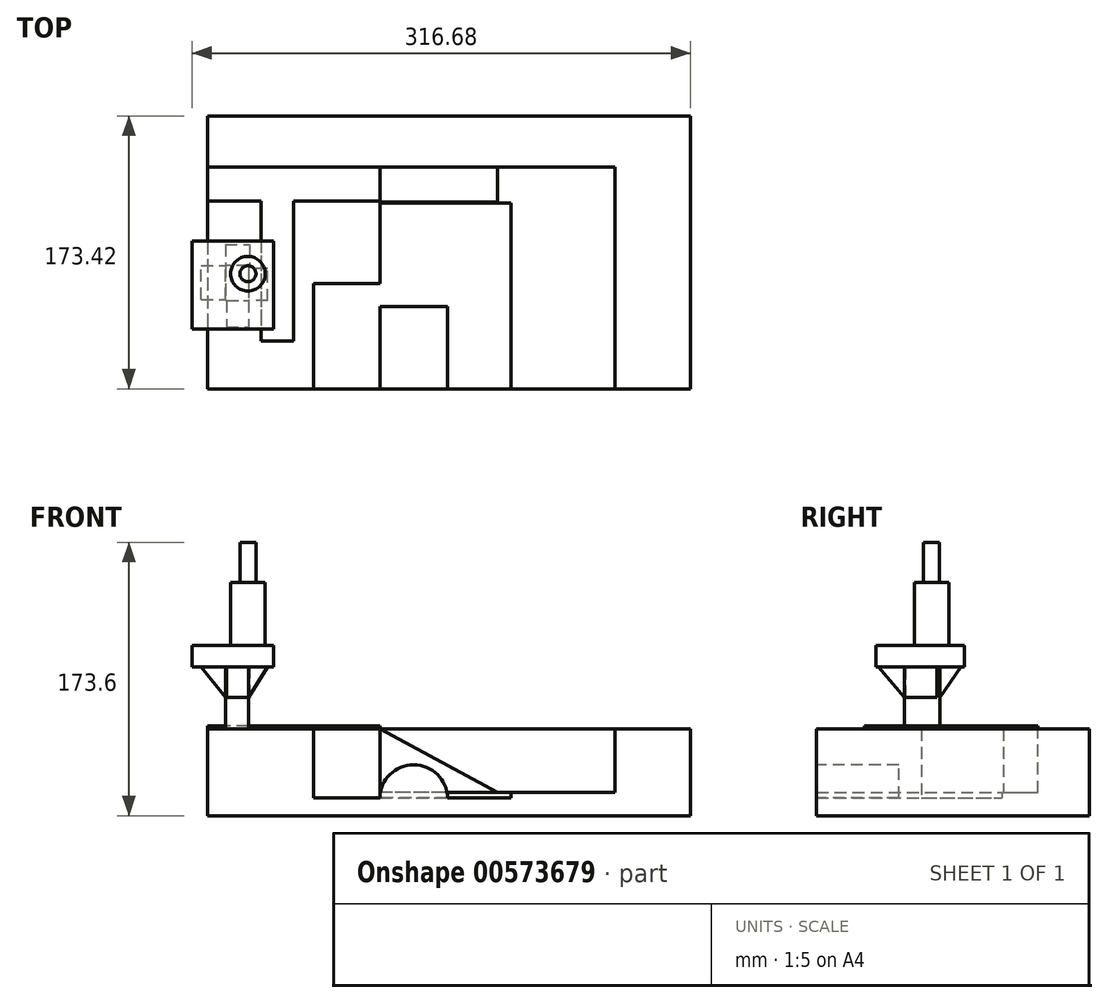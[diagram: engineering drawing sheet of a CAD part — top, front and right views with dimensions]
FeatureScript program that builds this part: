
annotation { "Feature Type Name" : "Feature", "Feature Type Description" : "" }
export const myFeature = defineFeature(function(context is Context, id is Id, definition is map)
    precondition{}
    {
        {
            var Q0;
            Q0=qCreatedBy(makeId("Top.planeOp"),FACE);
            var sketch = newSketch(context, id + "F0", { "sketchPlane" : qUnion([Q0])});
            skLineSegment(sketch, "E0.bottom", {"start": v(-152.49, 87.75) * mm, "end": v(154.33, 87.75) * mm});
            skLineSegment(sketch, "E0.top", {"start": v(-152.49, -85.67) * mm, "end": v(154.33, -85.67) * mm});
            skLineSegment(sketch, "E0.left", {"start": v(-152.49, 87.75) * mm, "end": v(-152.49, -85.67) * mm});
            skLineSegment(sketch, "E0.right", {"start": v(154.33, 87.75) * mm, "end": v(154.33, -85.67) * mm});
            skSolve(sketch);
        }
        {
            var Q0;
            Q0=makeQuery(id+"F0.imprint","IMPRINT",FACE,{"disambiguationData":[TD([[makeQuery(id+"F0.imprint","IMPRINT",EDGE,{"derivedFrom":sQuery(id+"F0.wireOp",EDGE,"E0.bottom")}),-1.0]])]});
            extrude(context, id + "F1", {"entities" : qUnion([Q0]), "depth" : 11.18 * mm, "offsetDistance" : 25.4 * mm});
        }
        {
            var Q0;
            Q0=makeQuery(id+"F1.opExtrude","SWEPT_FACE",FACE,{"disambiguationData":[OSD([sQuery(id+"F0.wireOp",EDGE,"E0.top")])]});
            var sketch = newSketch(context, id + "F2", { "sketchPlane" : qUnion([Q0])});
            skArc(sketch, "E1", {"start": v(-107.61, 11.18) * mm, "mid": v(-130.05, 33.61) * mm, "end": v(-152.49, 11.18) * mm});
            skArc(sketch, "E2", {"start": v(-55.5, 11.18) * mm, "mid": v(-74.45, 31.64) * mm, "end": v(-93.4, 11.18) * mm});
            skArc(sketch, "E3", {"start": v(0, 11.18) * mm, "mid": v(-21.5, 32.34) * mm, "end": v(-43, 11.18) * mm});
            skSolve(sketch);
        }
        {
            var Q0;
            {var subQ0=sQuery(id+"F2.wireOp",EDGE,"E3");Q0=makeQuery(id+"F2.imprint","IMPRINT",FACE,{"disambiguationData":[TD([[makeQuery(id+"F2.imprint","IMPRINT",EDGE,{"derivedFrom":subQ0}),1.0]])]});}
            extrude(context, id + "F3", {"entities" : qUnion([Q0]), "operationType" : NewBodyOperationType.ADD, "oppositeDirection" : true, "depth" : 52.32 * mm, "offsetDistance" : 25.4 * mm});
        }
        {
            var Q0;
            Q0=makeQuery(id+"F1.opExtrude","CAP_FACE",FACE,{"disambiguationData":[OSD([sQuery(id+"F0.wireOp",EDGE,"E0.bottom"),sQuery(id+"F0.wireOp",EDGE,"E0.top"),sQuery(id+"F0.wireOp",EDGE,"E0.left"),sQuery(id+"F0.wireOp",EDGE,"E0.right")])],"isStart":false});
            var sketch = newSketch(context, id + "F4", { "sketchPlane" : qUnion([Q0])});
            skLineSegment(sketch, "E4.bottom", {"start": v(40.35, -85.67) * mm, "end": v(106.46, -85.67) * mm});
            skLineSegment(sketch, "E4.top", {"start": v(40.35, 32.21) * mm, "end": v(106.46, 32.21) * mm});
            skLineSegment(sketch, "E4.left", {"start": v(40.35, -85.67) * mm, "end": v(40.35, 32.21) * mm});
            skLineSegment(sketch, "E4.right", {"start": v(106.46, -85.67) * mm, "end": v(106.46, 32.21) * mm});
            skLineSegment(sketch, "E5.bottom", {"start": v(106.46, 32.21) * mm, "end": v(-42.97, 32.21) * mm});
            skLineSegment(sketch, "E5.top", {"start": v(106.46, 55.06) * mm, "end": v(-42.97, 55.06) * mm});
            skLineSegment(sketch, "E5.left", {"start": v(106.46, 32.21) * mm, "end": v(106.46, 55.06) * mm});
            skLineSegment(sketch, "E5.right", {"start": v(-42.97, 32.21) * mm, "end": v(-42.97, 55.06) * mm});
            skSolve(sketch);
        }
        {
            var Q0;
            Q0 = qSketchRegion(id + "F4", true);
            extrude(context, id + "F5", {"entities" : qUnion([Q0]), "operationType" : NewBodyOperationType.ADD, "depth" : 3.56 * mm, "offsetDistance" : 25.4 * mm});
        }
        {
            var Q0;
            Q0=makeQuery(id+"F1.opExtrude","CAP_FACE",FACE,{"disambiguationData":[OSD([sQuery(id+"F0.wireOp",EDGE,"E0.bottom"),sQuery(id+"F0.wireOp",EDGE,"E0.top"),sQuery(id+"F0.wireOp",EDGE,"E0.left"),sQuery(id+"F0.wireOp",EDGE,"E0.right")])],"isStart":false});
            var sketch = newSketch(context, id + "F6", { "sketchPlane" : qUnion([Q0])});
            skLineSegment(sketch, "E6", {"start": v(106.46, -85.67) * mm, "end": v(154.33, -85.67) * mm});
            skLineSegment(sketch, "E7", {"start": v(154.33, -85.67) * mm, "end": v(154.33, 87.75) * mm});
            skLineSegment(sketch, "E8", {"start": v(154.33, 87.75) * mm, "end": v(-152.49, 87.75) * mm});
            skLineSegment(sketch, "E9", {"start": v(-152.49, 87.75) * mm, "end": v(-152.49, -85.67) * mm});
            skLineSegment(sketch, "E10", {"start": v(-152.49, -85.67) * mm, "end": v(-85.11, -85.67) * mm});
            skLineSegment(sketch, "E11", {"start": v(-85.11, -85.67) * mm, "end": v(-85.11, -18.87) * mm});
            skLineSegment(sketch, "E12", {"start": v(-85.11, -18.87) * mm, "end": v(-43, -18.87) * mm});
            skLineSegment(sketch, "E13", {"start": v(-43, -18.87) * mm, "end": v(-42.97, 32.21) * mm});
            skLineSegment(sketch, "E14", {"start": v(-42.97, 32.21) * mm, "end": v(-42.97, 55.06) * mm});
            skLineSegment(sketch, "E15", {"start": v(-42.97, 55.06) * mm, "end": v(106.46, 55.06) * mm});
            skLineSegment(sketch, "E16", {"start": v(106.46, 55.06) * mm, "end": v(106.46, -85.67) * mm});
            skSolve(sketch);
        }
        {
            var Q0;
            Q0 = qSketchRegion(id + "F6", true);
            extrude(context, id + "F7", {"entities" : qUnion([Q0]), "operationType" : NewBodyOperationType.ADD, "depth" : 43.94 * mm, "offsetDistance" : 25.4 * mm});
        }
        {
            var Q0;
            Q0=makeQuery(id+"F7.opExtrude","SWEPT_FACE",FACE,{"disambiguationData":[OSD([sQuery(id+"F6.wireOp",EDGE,"E15")])]});
            var sketch = newSketch(context, id + "F8", { "sketchPlane" : qUnion([Q0])});
            skLineSegment(sketch, "E17", {"start": v(31.75, 14.73) * mm, "end": v(-42.97, 55.12) * mm});
            skLineSegment(sketch, "E18", {"start": v(-42.97, 55.12) * mm, "end": v(-42.97, 14.73) * mm});
            skLineSegment(sketch, "E19", {"start": v(-42.97, 14.73) * mm, "end": v(31.75, 14.73) * mm});
            skSolve(sketch);
        }
        {
            var Q0;
            Q0 = qSketchRegion(id + "F8", true);
            extrude(context, id + "F9", {"entities" : qUnion([Q0]), "operationType" : NewBodyOperationType.ADD, "depth" : 22.1 * mm, "offsetDistance" : 25.4 * mm});
        }
        {
            var Q0;
            Q0=makeQuery(id+"F7.opExtrude","CAP_FACE",FACE,{"disambiguationData":[OSD([sQuery(id+"F6.wireOp",EDGE,"E6"),sQuery(id+"F6.wireOp",EDGE,"E7"),sQuery(id+"F6.wireOp",EDGE,"E8"),sQuery(id+"F6.wireOp",EDGE,"E9"),sQuery(id+"F6.wireOp",EDGE,"E10"),sQuery(id+"F6.wireOp",EDGE,"E11"),sQuery(id+"F6.wireOp",EDGE,"E12"),sQuery(id+"F6.wireOp",EDGE,"E13"),sQuery(id+"F6.wireOp",EDGE,"E14"),sQuery(id+"F6.wireOp",EDGE,"E15"),sQuery(id+"F6.wireOp",EDGE,"E16")])],"isStart":false});
            var sketch = newSketch(context, id + "F10", { "sketchPlane" : qUnion([Q0])});
            skLineSegment(sketch, "E20.bottom", {"start": v(-42.97, 55.06) * mm, "end": v(-152.49, 55.06) * mm});
            skLineSegment(sketch, "E20.top", {"start": v(-42.97, 33.55) * mm, "end": v(-152.49, 33.55) * mm});
            skLineSegment(sketch, "E20.left", {"start": v(-42.97, 55.06) * mm, "end": v(-42.97, 33.55) * mm});
            skLineSegment(sketch, "E20.right", {"start": v(-152.49, 55.06) * mm, "end": v(-152.49, 33.55) * mm});
            skLineSegment(sketch, "E21.bottom", {"start": v(-97.73, 33.55) * mm, "end": v(-118.38, 33.55) * mm});
            skLineSegment(sketch, "E21.top", {"start": v(-97.73, -55.17) * mm, "end": v(-118.38, -55.17) * mm});
            skLineSegment(sketch, "E21.left", {"start": v(-97.73, 33.55) * mm, "end": v(-97.73, -55.17) * mm});
            skLineSegment(sketch, "E21.right", {"start": v(-118.38, 33.55) * mm, "end": v(-118.38, -55.17) * mm});
            skSolve(sketch);
        }
        {
            var Q0;
            Q0 = qSketchRegion(id + "F10", true);
            extrude(context, id + "F11", {"entities" : qUnion([Q0]), "operationType" : NewBodyOperationType.ADD, "depth" : 2.03 * mm, "offsetDistance" : 25.4 * mm});
        }
        {
            var Q0;
            {var subQ0=sQuery(id+"F6.wireOp",EDGE,"E13");var subQ2=sQuery(id+"F6.wireOp",EDGE,"E12");var subQ4=sQuery(id+"F6.wireOp",EDGE,"E11");var subQ6=sQuery(id+"F6.wireOp",EDGE,"E9");var subQ9=sQuery(id+"F6.wireOp",EDGE,"E6");var subQ11=sQuery(id+"F6.wireOp",EDGE,"E10");var subQ14=sQuery(id+"F6.wireOp",EDGE,"E15");var subQ15=sQuery(id+"F6.wireOp",EDGE,"E14");Q0=makeQuery(id+"F11.boolean.opBoolean","SPLIT",FACE,{"disambiguationData":[TD([makeQuery(id+"F7.opExtrude","SWEPT_FACE",FACE,{"disambiguationData":[OSD([subQ4])]})])],"derivedFrom":makeQuery(id+"F7.opExtrude","CAP_FACE",FACE,{"disambiguationData":[OSD([subQ9,sQuery(id+"F6.wireOp",EDGE,"E7"),sQuery(id+"F6.wireOp",EDGE,"E8"),subQ6,subQ11,subQ4,subQ2,subQ0,subQ15,subQ14,sQuery(id+"F6.wireOp",EDGE,"E16")])],"isStart":false})});}
            var sketch = newSketch(context, id + "F12", { "sketchPlane" : qUnion([Q0])});
            skLineSegment(sketch, "E22.bottom", {"start": v(-141.1, -7.33) * mm, "end": v(-126.35, -7.33) * mm});
            skLineSegment(sketch, "E22.top", {"start": v(-141.1, -29.66) * mm, "end": v(-126.35, -29.66) * mm});
            skLineSegment(sketch, "E22.left", {"start": v(-141.1, -7.33) * mm, "end": v(-141.1, -29.66) * mm});
            skLineSegment(sketch, "E22.right", {"start": v(-126.35, -7.33) * mm, "end": v(-126.35, -29.66) * mm});
            skSolve(sketch);
        }
        {
            var Q0;
            Q0 = qSketchRegion(id + "F12", true);
            extrude(context, id + "F13", {"entities" : qUnion([Q0]), "operationType" : NewBodyOperationType.ADD, "depth" : 40.13 * mm, "offsetDistance" : 25.4 * mm});
        }
        {
            var Q0;
            Q0=makeQuery(id+"F13.opExtrude","SWEPT_FACE",FACE,{"disambiguationData":[OSD([sQuery(id+"F12.wireOp",EDGE,"E22.right")])]});
            var sketch = newSketch(context, id + "F14", { "sketchPlane" : qUnion([Q0])});
            skLineSegment(sketch, "E23", {"start": v(-29.66, 75.18) * mm, "end": v(-46.44, 94.76) * mm});
            skLineSegment(sketch, "E24", {"start": v(-46.44, 94.76) * mm, "end": v(-29.66, 95.25) * mm});
            skLineSegment(sketch, "E25", {"start": v(-29.66, 95.25) * mm, "end": v(-29.66, 75.18) * mm});
            skSolve(sketch);
        }
        {
            var Q0;
            Q0 = qSketchRegion(id + "F14", true);
            extrude(context, id + "F15", {"entities" : qUnion([Q0]), "operationType" : NewBodyOperationType.ADD, "oppositeDirection" : true, "depth" : 13.97 * mm, "offsetDistance" : 25.4 * mm});
        }
        {
            var Q0;
            Q0=makeQuery(id+"F13.opExtrude","SWEPT_FACE",FACE,{"disambiguationData":[OSD([sQuery(id+"F12.wireOp",EDGE,"E22.top")])]});
            var sketch = newSketch(context, id + "F16", { "sketchPlane" : qUnion([Q0])});
            skLineSegment(sketch, "E26", {"start": v(-126.35, 75.18) * mm, "end": v(-126.35, 96.3) * mm});
            skLineSegment(sketch, "E27", {"start": v(-126.35, 96.3) * mm, "end": v(-113.21, 96.3) * mm});
            skLineSegment(sketch, "E28", {"start": v(-113.21, 96.3) * mm, "end": v(-126.35, 75.18) * mm});
            skSolve(sketch);
        }
        {
            var Q0;
            Q0 = qSketchRegion(id + "F16", true);
            extrude(context, id + "F17", {"entities" : qUnion([Q0]), "operationType" : NewBodyOperationType.ADD, "oppositeDirection" : true, "depth" : 20.57 * mm, "offsetDistance" : 25.4 * mm});
        }
        {
            var Q0;
            Q0=makeQuery(id+"F13.opExtrude","SWEPT_FACE",FACE,{"disambiguationData":[OSD([sQuery(id+"F12.wireOp",EDGE,"E22.left")])]});
            var sketch = newSketch(context, id + "F18", { "sketchPlane" : qUnion([Q0])});
            skLineSegment(sketch, "E29", {"start": v(7.33, 95.25) * mm, "end": v(-6.39, 95.25) * mm});
            skLineSegment(sketch, "E30", {"start": v(-6.39, 95.25) * mm, "end": v(7.33, 75.18) * mm});
            skLineSegment(sketch, "E31", {"start": v(7.33, 75.18) * mm, "end": v(7.33, 95.25) * mm});
            skSolve(sketch);
        }
        {
            var Q0;
            Q0 = qSketchRegion(id + "F18", true);
            extrude(context, id + "F19", {"entities" : qUnion([Q0]), "operationType" : NewBodyOperationType.ADD, "oppositeDirection" : true, "depth" : 15.24 * mm, "offsetDistance" : 25.4 * mm});
        }
        {
            var Q0;
            Q0=makeQuery(id+"F13.opExtrude","SWEPT_FACE",FACE,{"disambiguationData":[OSD([sQuery(id+"F12.wireOp",EDGE,"E22.bottom")])]});
            var sketch = newSketch(context, id + "F20", { "sketchPlane" : qUnion([Q0])});
            skLineSegment(sketch, "E32", {"start": v(141.1, 75.18) * mm, "end": v(141.1, 94.6) * mm});
            skLineSegment(sketch, "E33", {"start": v(141.1, 94.6) * mm, "end": v(156.48, 94.6) * mm});
            skLineSegment(sketch, "E34", {"start": v(156.48, 94.6) * mm, "end": v(141.1, 75.18) * mm});
            skSolve(sketch);
        }
        {
            var Q0;
            Q0 = qSketchRegion(id + "F20", true);
            extrude(context, id + "F21", {"entities" : qUnion([Q0]), "operationType" : NewBodyOperationType.ADD, "oppositeDirection" : true, "depth" : 21.59 * mm, "offsetDistance" : 25.4 * mm});
        }
        {
            var Q0;
            Q0=makeQuery(id+"F21.opExtrude","SWEPT_FACE",FACE,{"disambiguationData":[OSD([sQuery(id+"F20.wireOp",EDGE,"E33")])]});
            var sketch = newSketch(context, id + "F22", { "sketchPlane" : qUnion([Q0])});
            skLineSegment(sketch, "E35.bottom", {"start": v(-162.35, -47.82) * mm, "end": v(-110.38, -47.82) * mm});
            skLineSegment(sketch, "E35.top", {"start": v(-162.35, 8.17) * mm, "end": v(-110.38, 8.17) * mm});
            skLineSegment(sketch, "E35.left", {"start": v(-162.35, -47.82) * mm, "end": v(-162.35, 8.17) * mm});
            skLineSegment(sketch, "E35.right", {"start": v(-110.38, -47.82) * mm, "end": v(-110.38, 8.17) * mm});
            skSolve(sketch);
        }
        {
            var Q0;
            Q0 = qSketchRegion(id + "F22", true);
            extrude(context, id + "F23", {"entities" : qUnion([Q0]), "operationType" : NewBodyOperationType.ADD, "depth" : 13.46 * mm, "offsetDistance" : 25.4 * mm});
        }
        {
            var Q0;
            Q0=makeQuery(id+"F23.opExtrude","CAP_FACE",FACE,{"disambiguationData":[OSD([sQuery(id+"F22.wireOp",EDGE,"E35.bottom"),sQuery(id+"F22.wireOp",EDGE,"E35.top"),sQuery(id+"F22.wireOp",EDGE,"E35.left"),sQuery(id+"F22.wireOp",EDGE,"E35.right")])],"isStart":false});
            var sketch = newSketch(context, id + "F24", { "sketchPlane" : qUnion([Q0])});
            skCircle(sketch, "E36", {"center": v(-126.76, -12.52) * mm, "radius": 10.97 * mm});
            skSolve(sketch);
        }
        {
            var Q0;
            Q0 = qSketchRegion(id + "F24", true);
            extrude(context, id + "F25", {"entities" : qUnion([Q0]), "operationType" : NewBodyOperationType.ADD, "depth" : 40.13 * mm, "offsetDistance" : 25.4 * mm});
        }
        {
            var Q0;
            Q0=makeQuery(id+"F25.opExtrude","CAP_FACE",FACE,{"disambiguationData":[OSD([sQuery(id+"F24.wireOp",EDGE,"E36")])],"isStart":false});
            var sketch = newSketch(context, id + "F26", { "sketchPlane" : qUnion([Q0])});
            skCircle(sketch, "E37", {"center": v(-126.76, -12.52) * mm, "radius": 5.07 * mm});
            skSolve(sketch);
        }
        {
            var Q0;
            Q0 = qSketchRegion(id + "F26", true);
            extrude(context, id + "F27", {"entities" : qUnion([Q0]), "operationType" : NewBodyOperationType.ADD, "depth" : 25.4 * mm, "offsetDistance" : 25.4 * mm});
        }
    });
